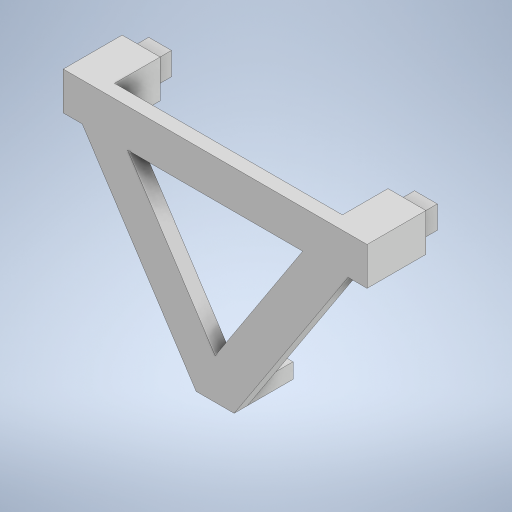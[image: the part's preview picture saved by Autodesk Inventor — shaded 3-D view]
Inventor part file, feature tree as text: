
AUTODESK INVENTOR PART (.ipt)
format: ipt  version: 2024 (Build 280153000, 153)  size: 300,032 bytes
history: native  units: in
note: dims shown in document units (in); Inventor stores cm internally (conversion verified against a paired STEP export)
features: extrude x4, sketch x2, chamfer x1
ambient origin geometry x8: Origin, YZ Plane, XZ Plane, XY Plane, X Axis, Y Axis, Z Axis, Center Point
bodies: Solid1 (feature_tree)
feature tree (7):
  sketch  "Sketch1"  dims[d0=1.1811in d1=1.5945in]
  extrude  "Extrusion1"  Depth=1.1811in
  extrude  "Extrusion2"  Depth=0.1969in
  extrude  "Extrusion3"  Depth=0.0787in
  extrude  "Extrusion4"  Depth=0.1969in
  chamfer  "Chamfer2"  Distance=0.0984in
  sketch  "Sketch3"  dims[d4=0.1969in d5=0.1969in d7=0.0787in d8=0.1969in d9=0.0984in d10=0.0689in d11=0.0in d12=0.9055in d13=0.2362in d14=0.0in d15=0.1969in d16=0.2362in d17=0.0in d23=0.0394in d24=0.0394in d25=0.1181in d26=0.0in d27=0.0197in d28=0.1969in d29=45.0deg d18=0.0344in]
